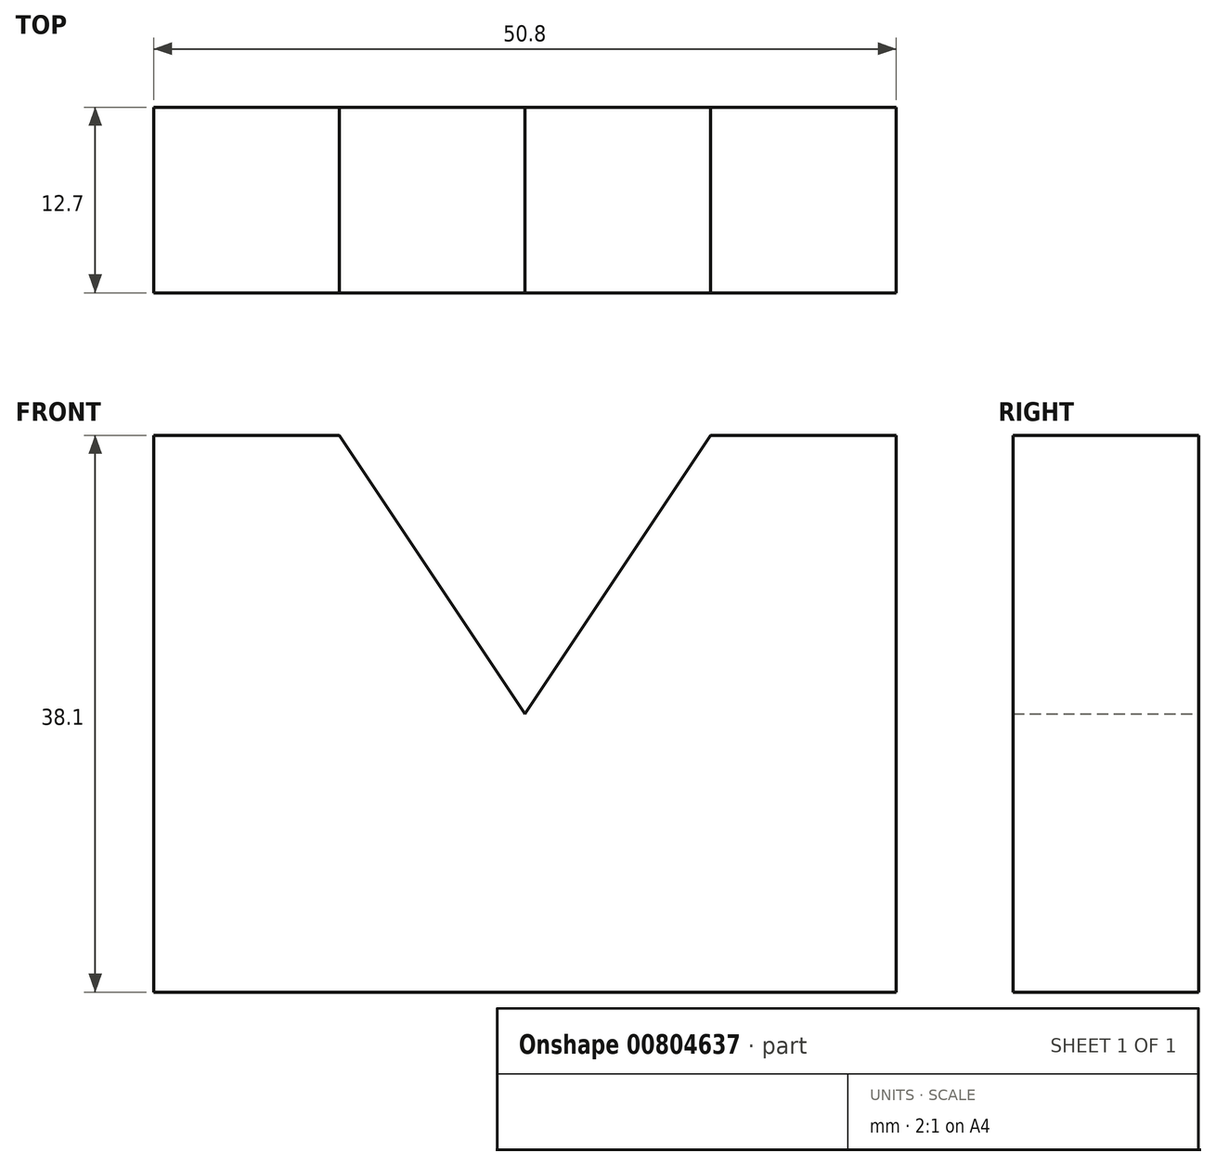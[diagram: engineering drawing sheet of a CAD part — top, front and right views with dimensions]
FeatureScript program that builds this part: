
annotation { "Feature Type Name" : "Feature", "Feature Type Description" : "" }
export const myFeature = defineFeature(function(context is Context, id is Id, definition is map)
    precondition{}
    {
        {
            var Q0;
            Q0=qCreatedBy(makeId("Front.planeOp"),FACE);
            var sketch = newSketch(context, id + "F0", { "sketchPlane" : qUnion([Q0])});
            skLineSegment(sketch, "E0", {"start": v(0, 0) * mm, "end": v(50.8, 0) * mm});
            skLineSegment(sketch, "E1", {"start": v(50.8, 0) * mm, "end": v(50.8, 38.1) * mm});
            skLineSegment(sketch, "E2", {"start": v(50.8, 38.1) * mm, "end": v(38.1, 38.1) * mm});
            skLineSegment(sketch, "E3", {"start": v(0, 0) * mm, "end": v(0, 38.1) * mm});
            skLineSegment(sketch, "E4", {"start": v(0, 38.1) * mm, "end": v(12.7, 38.1) * mm});
            skLineSegment(sketch, "E5", {"start": v(25.4, 0) * mm, "end": v(25.4, 19.05) * mm, "construction": true});
            skLineSegment(sketch, "E6", {"start": v(25.4, 19.05) * mm, "end": v(12.7, 38.1) * mm});
            skLineSegment(sketch, "E7", {"start": v(25.4, 19.05) * mm, "end": v(38.1, 38.1) * mm});
            skSolve(sketch);
        }
        {
            var Q0;
            Q0 = qSketchRegion(id + "F0", true);
            extrude(context, id + "F1", {"entities" : qUnion([Q0]), "depth" : 12.7 * mm, "offsetDistance" : 25.4 * mm});
        }
    });
